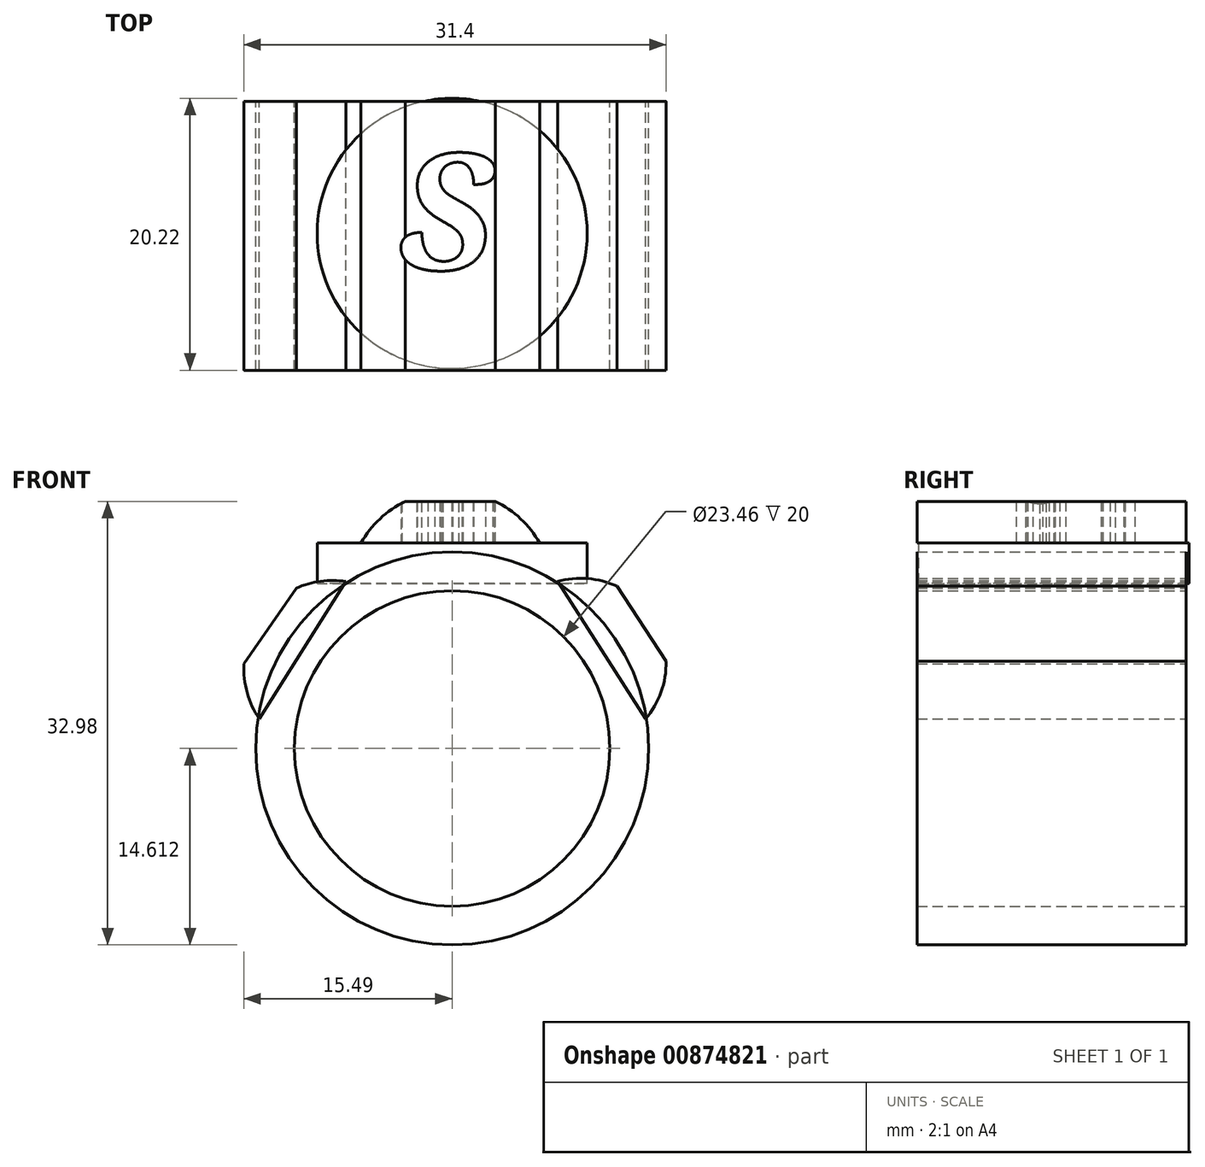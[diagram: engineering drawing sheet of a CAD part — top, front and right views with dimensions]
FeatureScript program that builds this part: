
annotation { "Feature Type Name" : "Feature", "Feature Type Description" : "" }
export const myFeature = defineFeature(function(context is Context, id is Id, definition is map)
    precondition{}
    {
        {
            var Q0;
            Q0=qCreatedBy(makeId("Front.planeOp"),FACE);
            var sketch = newSketch(context, id + "F0", { "sketchPlane" : qUnion([Q0])});
            skCircle(sketch, "E0", {"center": v(0, -15.27) * mm, "radius": 14.6 * mm});
            skCircle(sketch, "E1", {"center": v(0, -15.27) * mm, "radius": 11.73 * mm});
            skSolve(sketch);
        }
        {
            var Q0;
            Q0 = qSketchRegion(id + "F0", true);
            extrude(context, id + "F1", {"entities" : qUnion([Q0]), "depth" : 20 * mm, "offsetDistance" : 25 * mm});
        }
        {
            var Q0;
            Q0=qCreatedBy(makeId("Top.planeOp"),FACE);
            var sketch = newSketch(context, id + "F2", { "sketchPlane" : qUnion([Q0])});
            skCircle(sketch, "E2", {"center": v(0, -9.83) * mm, "radius": 10.04 * mm});
            skSolve(sketch);
        }
        {
            var Q0;
            Q0 = qSketchRegion(id + "F2", true);
            extrude(context, id + "F3", {"entities" : qUnion([Q0]), "oppositeDirection" : true, "depth" : 3 * mm, "offsetDistance" : 25 * mm});
        }
        {
            var Q0;
            Q0=qCreatedBy(makeId("Front.planeOp"),FACE);
            var sketch = newSketch(context, id + "F4", { "sketchPlane" : qUnion([Q0])});
            skArc(sketch, "E3", {"start": v(6.5, 0) * mm, "mid": v(5.1, 1.8) * mm, "end": v(3.21, 3.1) * mm});
            skLineSegment(sketch, "E4", {"start": v(-3.49, 3.1) * mm, "end": v(3.21, 3.1) * mm});
            skArc(sketch, "E5.trimOffspring", {"start": v(-3.49, 3.1) * mm, "mid": v(-5.37, 1.8) * mm, "end": v(-6.79, 0) * mm});
            skLineSegment(sketch, "E6", {"start": v(-6.79, 0) * mm, "end": v(6.5, 0) * mm});
            skSolve(sketch);
        }
        {
            var Q0;
            Q0 = qSketchRegion(id + "F4", true);
            extrude(context, id + "F5", {"entities" : qUnion([Q0]), "operationType" : NewBodyOperationType.ADD, "depth" : 20 * mm, "offsetDistance" : 25 * mm});
        }
        {
            var Q0;
            Q0=qCreatedBy(makeId("Front.planeOp"),FACE);
            var sketch = newSketch(context, id + "F6", { "sketchPlane" : qUnion([Q0])});
            skArc(sketch, "E7", {"start": v(-7.9, -2.86) * mm, "mid": v(-9.78, -2.84) * mm, "end": v(-11.6, -3.35) * mm});
            skArc(sketch, "E8", {"start": v(14.38, -13.08) * mm, "mid": v(15.54, -11.07) * mm, "end": v(15.9, -8.79) * mm});
            skLineSegment(sketch, "E9", {"start": v(-11.6, -3.35) * mm, "end": v(-15.48, -8.99) * mm});
            skLineSegment(sketch, "E10", {"start": v(-14.33, -13.08) * mm, "end": v(-7.9, -2.86) * mm});
            skArc(sketch, "E11.trimOffspring", {"start": v(-15.48, -8.99) * mm, "mid": v(-15.24, -11.13) * mm, "end": v(-14.33, -13.08) * mm});
            skLineSegment(sketch, "E12", {"start": v(12.26, -3.21) * mm, "end": v(15.9, -8.79) * mm});
            skArc(sketch, "E13.trimOffspring", {"start": v(12.26, -3.21) * mm, "mid": v(10.08, -2.64) * mm, "end": v(7.84, -2.86) * mm});
            skLineSegment(sketch, "E14", {"start": v(7.84, -2.86) * mm, "end": v(14.38, -13.08) * mm});
            skSolve(sketch);
        }
        {
            var Q0;
            Q0 = qSketchRegion(id + "F6", true);
            extrude(context, id + "F7", {"entities" : qUnion([Q0]), "depth" : 20 * mm, "offsetDistance" : 25 * mm});
        }
        {
            var Q0;
            Q0=qCreatedBy(makeId("Top.planeOp"),FACE);
            var sketch = newSketch(context, id + "F8", { "sketchPlane" : qUnion([Q0])});
            skText(sketch, "E15", { "text": "S\n", "fontName": "NotoSerif-BoldItalic.ttf"});
            const initialGuessF8  = {"E15": [-0.00398, -0.01252, 1, 0, 0.00867]};
            skSetInitialGuess(sketch, initialGuessF8);
            skSolve(sketch);
        }
        {
            var Q0;
            Q0 = qSketchRegion(id + "F8", true);
            extrude(context, id + "F9", {"entities" : qUnion([Q0]), "operationType" : NewBodyOperationType.REMOVE, "depth" : 60 * mm, "offsetDistance" : 25 * mm});
        }
    });
